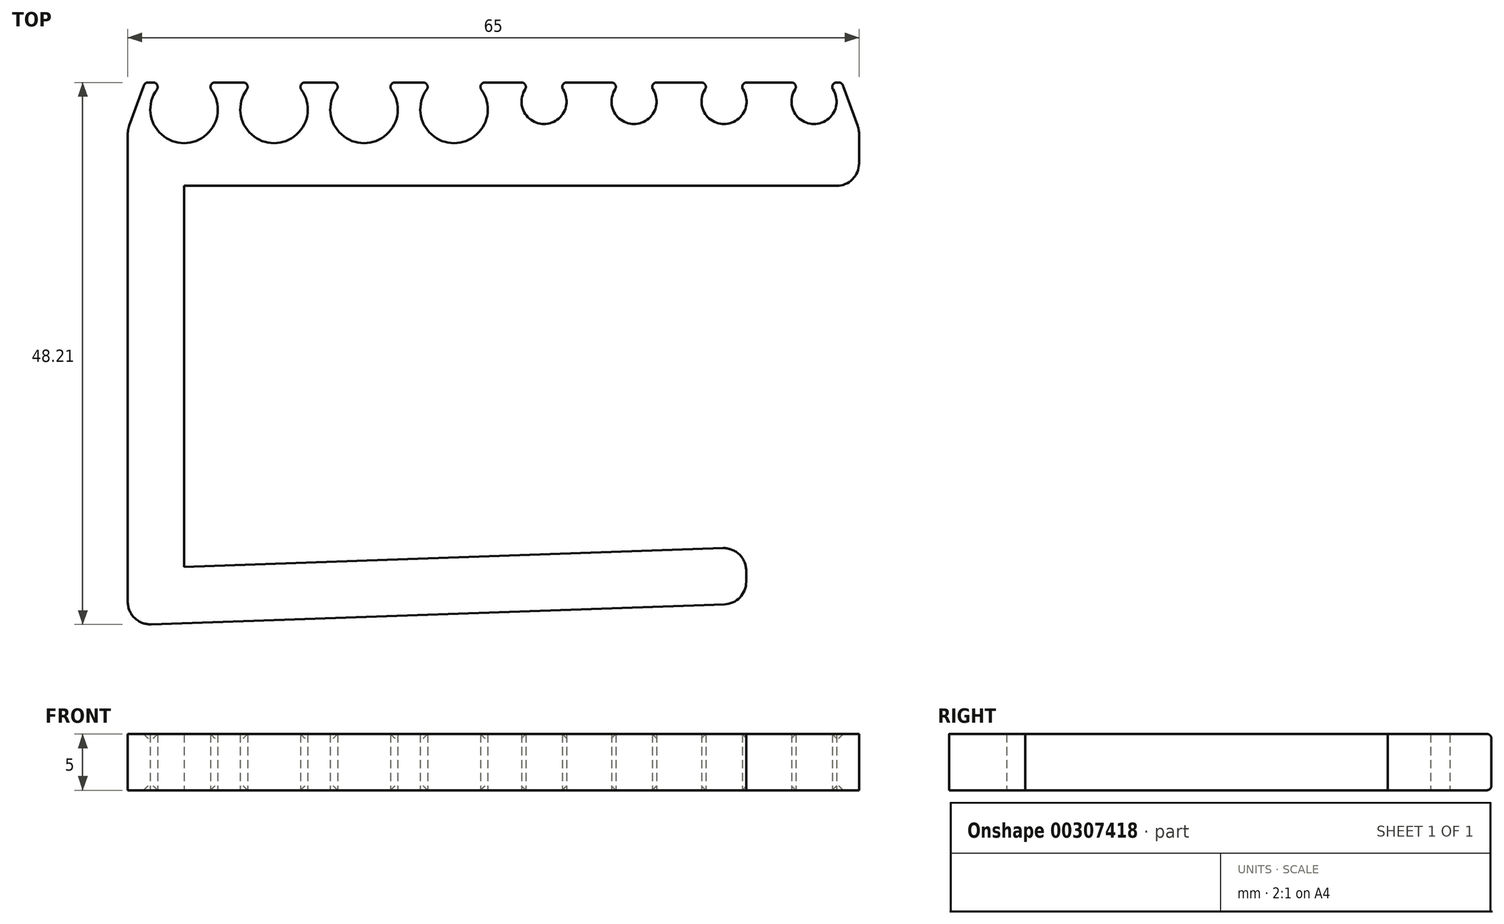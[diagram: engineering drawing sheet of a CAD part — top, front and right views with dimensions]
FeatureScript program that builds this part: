
annotation { "Feature Type Name" : "Feature", "Feature Type Description" : "" }
export const myFeature = defineFeature(function(context is Context, id is Id, definition is map)
    precondition{}
    {
        {
            var Q0;
            Q0=qCreatedBy(makeId("Top.planeOp"),FACE);
            var sketch = newSketch(context, id + "F0", { "sketchPlane" : qUnion([Q0])});
            skLineSegment(sketch, "E0", {"start": v(0, 0) * mm, "end": v(49.97, 1.74) * mm});
            skLineSegment(sketch, "E1", {"start": v(0, 0) * mm, "end": v(0, 33.9) * mm});
            skLineSegment(sketch, "E2", {"start": v(0, 33.9) * mm, "end": v(60, 33.9) * mm});
            skLineSegment(sketch, "E3", {"start": v(49.97, 1.74) * mm, "end": v(49.97, -3.26) * mm});
            skLineSegment(sketch, "E4", {"start": v(49.97, -3.26) * mm, "end": v(-5, -5.18) * mm});
            skLineSegment(sketch, "E5", {"start": v(-5, -5.18) * mm, "end": v(-5, 38.9) * mm});
            skLineSegment(sketch, "E6", {"start": v(-5, 38.9) * mm, "end": v(60, 38.9) * mm, "construction": true});
            skLineSegment(sketch, "E7", {"start": v(60, 38.9) * mm, "end": v(60, 33.9) * mm});
            skArc(sketch, "E8", {"start": v(-1.8, 43.1) * mm, "mid": v(0, 37.7) * mm, "end": v(1.8, 43.1) * mm});
            skArc(sketch, "E9", {"start": v(6.2, 43.1) * mm, "mid": v(8, 37.7) * mm, "end": v(9.8, 43.1) * mm});
            skArc(sketch, "E10", {"start": v(14.2, 43.1) * mm, "mid": v(16, 37.7) * mm, "end": v(17.8, 43.1) * mm});
            skArc(sketch, "E11", {"start": v(30.95, 43.1) * mm, "mid": v(32, 39.4) * mm, "end": v(33.05, 43.1) * mm});
            skArc(sketch, "E12", {"start": v(22.2, 43.1) * mm, "mid": v(24, 37.7) * mm, "end": v(25.8, 43.1) * mm});
            skArc(sketch, "E13", {"start": v(38.95, 43.1) * mm, "mid": v(40, 39.4) * mm, "end": v(41.05, 43.1) * mm});
            skArc(sketch, "E14", {"start": v(46.95, 43.1) * mm, "mid": v(48, 39.4) * mm, "end": v(49.05, 43.1) * mm});
            skArc(sketch, "E15", {"start": v(54.95, 43.1) * mm, "mid": v(56, 39.4) * mm, "end": v(57.05, 43.1) * mm});
            skLineSegment(sketch, "E16", {"start": v(0, 40.7) * mm, "end": v(8, 40.7) * mm, "construction": true});
            skLineSegment(sketch, "E17", {"start": v(8, 40.7) * mm, "end": v(16, 40.7) * mm, "construction": true});
            skLineSegment(sketch, "E18", {"start": v(16, 40.7) * mm, "end": v(24, 40.7) * mm, "construction": true});
            skLineSegment(sketch, "E19", {"start": v(32, 41.4) * mm, "end": v(40, 41.4) * mm, "construction": true});
            skLineSegment(sketch, "E20", {"start": v(40, 41.4) * mm, "end": v(48, 41.4) * mm, "construction": true});
            skLineSegment(sketch, "E21", {"start": v(48, 41.4) * mm, "end": v(56, 41.4) * mm, "construction": true});
            skLineSegment(sketch, "E22", {"start": v(1.8, 43.1) * mm, "end": v(6.2, 43.1) * mm});
            skLineSegment(sketch, "E23", {"start": v(-1.8, 43.1) * mm, "end": v(-3.47, 43.1) * mm});
            skLineSegment(sketch, "E24", {"start": v(-3.47, 43.1) * mm, "end": v(-5, 38.9) * mm});
            skLineSegment(sketch, "E25", {"start": v(58.47, 43.1) * mm, "end": v(60, 38.9) * mm});
            skLineSegment(sketch, "E26.trimOffspring", {"start": v(9.8, 43.1) * mm, "end": v(14.2, 43.1) * mm});
            skLineSegment(sketch, "E27.trimOffspring", {"start": v(17.8, 43.1) * mm, "end": v(22.2, 43.1) * mm});
            skLineSegment(sketch, "E28.trimOffspring", {"start": v(25.8, 43.1) * mm, "end": v(30.95, 43.1) * mm});
            skLineSegment(sketch, "E29.trimOffspring", {"start": v(33.05, 43.1) * mm, "end": v(38.95, 43.1) * mm});
            skLineSegment(sketch, "E30.trimOffspring", {"start": v(41.05, 43.1) * mm, "end": v(46.95, 43.1) * mm});
            skLineSegment(sketch, "E31.trimOffspring", {"start": v(49.05, 43.1) * mm, "end": v(54.95, 43.1) * mm});
            skLineSegment(sketch, "E32.trimOffspring", {"start": v(57.05, 43.1) * mm, "end": v(58.47, 43.1) * mm});
            skLineSegment(sketch, "E33", {"start": v(32, 41.4) * mm, "end": v(32, 40.7) * mm, "construction": true});
            skLineSegment(sketch, "E34", {"start": v(32, 40.7) * mm, "end": v(24, 40.7) * mm, "construction": true});
            skSolve(sketch);
        }
        {
            var Q0;
            Q0=makeQuery(id+"F0.imprint","IMPRINT",FACE,{"disambiguationData":[TD([[makeQuery(id+"F0.imprint","IMPRINT",EDGE,{"derivedFrom":sQuery(id+"F0.wireOp",EDGE,"E0")}),-1.0]])]});
            extrude(context, id + "F1", {"entities" : qUnion([Q0]), "depth" : 5 * mm});
        }
        {
            var Q0;
            Q0=makeQuery(id+"F1.opExtrude","SWEPT_EDGE",EDGE,{"disambiguationData":[OSD([sQuery(id+"F0.wireOp",EDGE,"E0"),sQuery(id+"F0.wireOp",EDGE,"E3")])]});
            var Q1;
            Q1=makeQuery(id+"F1.opExtrude","SWEPT_EDGE",EDGE,{"disambiguationData":[OSD([sQuery(id+"F0.wireOp",EDGE,"E3"),sQuery(id+"F0.wireOp",EDGE,"E4")])]});
            var Q2;
            Q2=makeQuery(id+"F1.opExtrude","SWEPT_EDGE",EDGE,{"disambiguationData":[OSD([sQuery(id+"F0.wireOp",EDGE,"E4"),sQuery(id+"F0.wireOp",EDGE,"E5")])]});
            var Q3;
            Q3=makeQuery(id+"F1.opExtrude","SWEPT_EDGE",EDGE,{"disambiguationData":[OSD([sQuery(id+"F0.wireOp",EDGE,"E5"),sQuery(id+"F0.wireOp",EDGE,"E24")])]});
            var Q4;
            Q4=makeQuery(id+"F1.opExtrude","SWEPT_EDGE",EDGE,{"disambiguationData":[OSD([sQuery(id+"F0.wireOp",EDGE,"E2"),sQuery(id+"F0.wireOp",EDGE,"E7")])]});
            var Q5;
            Q5=makeQuery(id+"F1.opExtrude","SWEPT_EDGE",EDGE,{"disambiguationData":[OSD([sQuery(id+"F0.wireOp",EDGE,"E7"),sQuery(id+"F0.wireOp",EDGE,"E25")])]});
            fillet(context, id + "F2", {"entities" : qUnion([Q0, Q1, Q2, Q3, Q4, Q5]), "radius" : 2 * mm, "tangentPropagation" : true, "allowEdgeOverflow" : false});
        }
        {
            var Q0;
            Q0=makeQuery(id+"F1.opExtrude","SWEPT_FACE",FACE,{"disambiguationData":[OSD([sQuery(id+"F0.wireOp",EDGE,"E23")])]});
            var Q1;
            Q1=makeQuery(id+"F1.opExtrude","SWEPT_FACE",FACE,{"disambiguationData":[OSD([sQuery(id+"F0.wireOp",EDGE,"E22")])]});
            var Q2;
            Q2=makeQuery(id+"F1.opExtrude","SWEPT_FACE",FACE,{"disambiguationData":[OSD([sQuery(id+"F0.wireOp",EDGE,"E26.trimOffspring")])]});
            var Q3;
            Q3=makeQuery(id+"F1.opExtrude","SWEPT_FACE",FACE,{"disambiguationData":[OSD([sQuery(id+"F0.wireOp",EDGE,"E27.trimOffspring")])]});
            var Q4;
            Q4=makeQuery(id+"F1.opExtrude","SWEPT_FACE",FACE,{"disambiguationData":[OSD([sQuery(id+"F0.wireOp",EDGE,"E28.trimOffspring")])]});
            var Q5;
            Q5=makeQuery(id+"F1.opExtrude","SWEPT_FACE",FACE,{"disambiguationData":[OSD([sQuery(id+"F0.wireOp",EDGE,"E29.trimOffspring")])]});
            var Q6;
            Q6=makeQuery(id+"F1.opExtrude","SWEPT_FACE",FACE,{"disambiguationData":[OSD([sQuery(id+"F0.wireOp",EDGE,"E30.trimOffspring")])]});
            var Q7;
            Q7=makeQuery(id+"F1.opExtrude","SWEPT_FACE",FACE,{"disambiguationData":[OSD([sQuery(id+"F0.wireOp",EDGE,"E31.trimOffspring")])]});
            var Q8;
            Q8=makeQuery(id+"F1.opExtrude","SWEPT_FACE",FACE,{"disambiguationData":[OSD([sQuery(id+"F0.wireOp",EDGE,"E32.trimOffspring")])]});
            fillet(context, id + "F3", {"entities" : qUnion([Q0, Q1, Q2, Q3, Q4, Q5, Q6, Q7, Q8]), "radius" : 0.4 * mm, "tangentPropagation" : true, "allowEdgeOverflow" : false});
        }
    });
